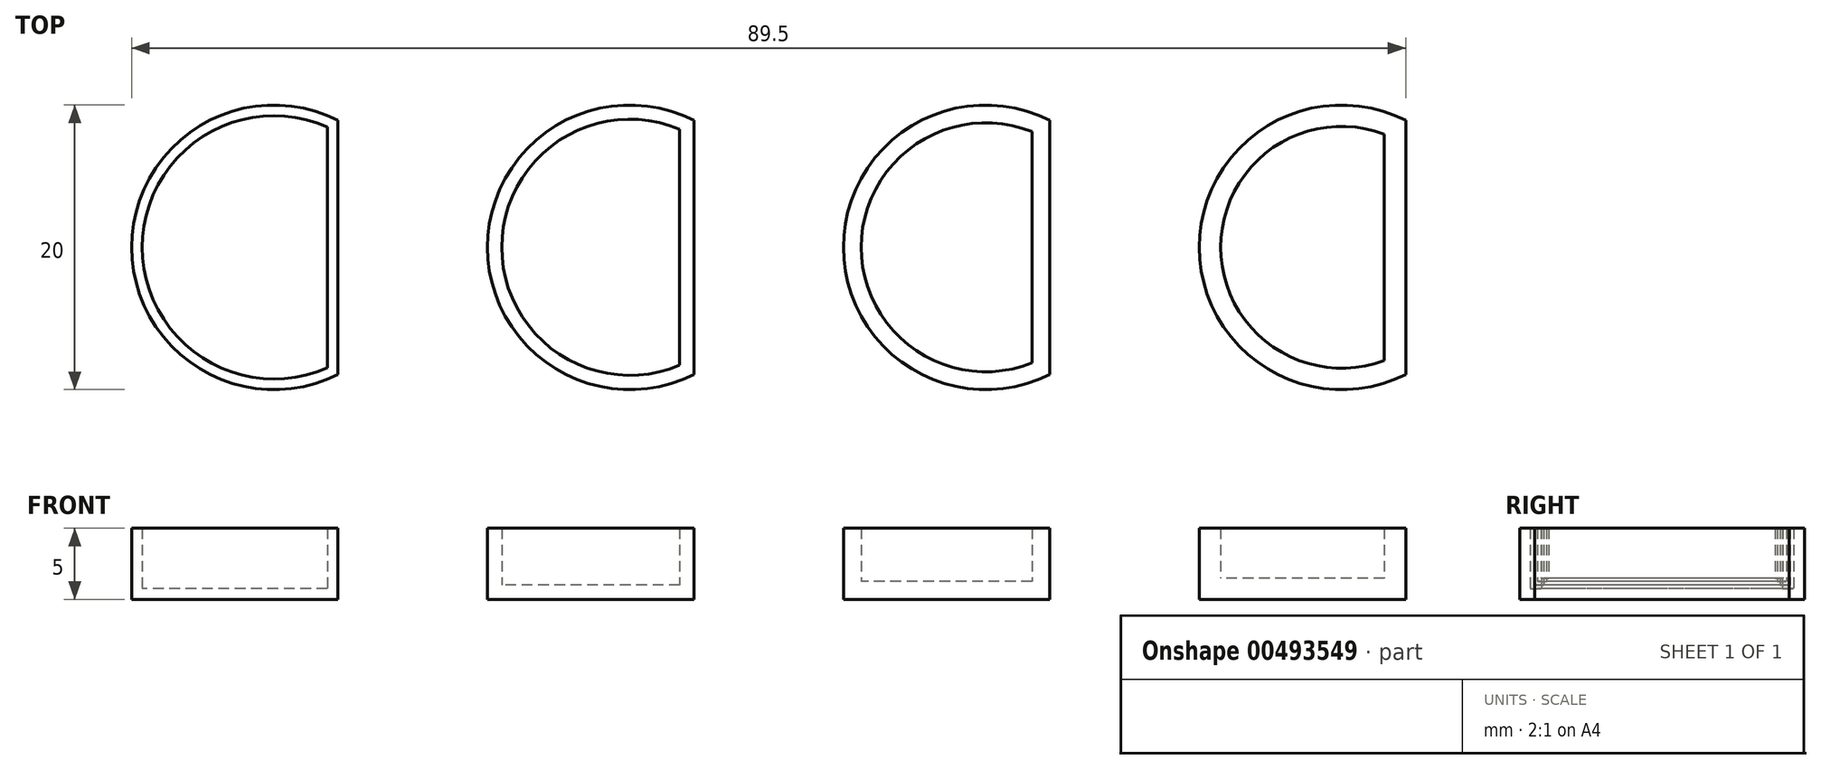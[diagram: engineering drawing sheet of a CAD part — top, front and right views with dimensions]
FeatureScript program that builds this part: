
annotation { "Feature Type Name" : "Feature", "Feature Type Description" : "" }
export const myFeature = defineFeature(function(context is Context, id is Id, definition is map)
    precondition{}
    {
        {
            var Q0;
            Q0=qCreatedBy(makeId("Top.planeOp"),FACE);
            var sketch = newSketch(context, id + "F0", { "sketchPlane" : qUnion([Q0])});
            skArc(sketch, "E0", {"start": v(-49.83, 50.8) * mm, "mid": v(-64.33, 41.87) * mm, "end": v(-49.83, 32.94) * mm});
            skLineSegment(sketch, "E1", {"start": v(-49.83, 50.8) * mm, "end": v(-49.83, 32.94) * mm});
            skArc(sketch, "E2.1.0.0", {"start": v(-24.83, 50.8) * mm, "mid": v(-39.33, 41.87) * mm, "end": v(-24.83, 32.94) * mm});
            skLineSegment(sketch, "E2.1.0.1", {"start": v(-24.83, 50.8) * mm, "end": v(-24.83, 32.94) * mm});
            skArc(sketch, "E2.2.0.0", {"start": v(0.17, 50.8) * mm, "mid": v(-14.33, 41.87) * mm, "end": v(0.17, 32.94) * mm});
            skLineSegment(sketch, "E2.2.0.1", {"start": v(0.17, 50.8) * mm, "end": v(0.17, 32.94) * mm});
            skArc(sketch, "E2.3.0.0", {"start": v(25.17, 50.8) * mm, "mid": v(10.67, 41.87) * mm, "end": v(25.17, 32.94) * mm});
            skLineSegment(sketch, "E2.3.0.1", {"start": v(25.17, 50.8) * mm, "end": v(25.17, 32.94) * mm});
            skLineSegment(sketch, "E2.direction1", {"start": v(-49.83, 32.94) * mm, "end": v(-24.83, 32.94) * mm, "construction": true});
            skSolve(sketch);
        }
        {
            var Q0;
            Q0=makeQuery(id+"F0.imprint","IMPRINT",FACE,{"disambiguationData":[TD([[makeQuery(id+"F0.imprint","IMPRINT",EDGE,{"derivedFrom":sQuery(id+"F0.wireOp",EDGE,"E0")}),1.0]])]});
            var Q1;
            Q1=makeQuery(id+"F0.imprint","IMPRINT",FACE,{"disambiguationData":[TD([[makeQuery(id+"F0.imprint","IMPRINT",EDGE,{"derivedFrom":sQuery(id+"F0.wireOp",EDGE,"E2.1.0.0")}),1.0]])]});
            var Q2;
            Q2=makeQuery(id+"F0.imprint","IMPRINT",FACE,{"disambiguationData":[TD([[makeQuery(id+"F0.imprint","IMPRINT",EDGE,{"derivedFrom":sQuery(id+"F0.wireOp",EDGE,"E2.2.0.0")}),1.0]])]});
            var Q3;
            Q3=makeQuery(id+"F0.imprint","IMPRINT",FACE,{"disambiguationData":[TD([[makeQuery(id+"F0.imprint","IMPRINT",EDGE,{"derivedFrom":sQuery(id+"F0.wireOp",EDGE,"E2.3.0.0")}),1.0]])]});
            extrude(context, id + "F1", {"entities" : qUnion([Q0, Q1, Q2, Q3]), "depth" : 5 * mm});
        }
        {
            var Q0;
            Q0=makeQuery(id+"F1.opExtrude","CAP_FACE",FACE,{"disambiguationData":[OSD([sQuery(id+"F0.wireOp",EDGE,"E0"),sQuery(id+"F0.wireOp",EDGE,"E1")])],"isStart":false});
            shell(context, id + "F2", {"entities" : qUnion([Q0]), "thickness" : .75 * mm});
        }
        {
            var Q0;
            Q0=makeQuery(id+"F1.opExtrude","CAP_FACE",FACE,{"disambiguationData":[OSD([sQuery(id+"F0.wireOp",EDGE,"E2.1.0.0"),sQuery(id+"F0.wireOp",EDGE,"E2.1.0.1")])],"isStart":false});
            shell(context, id + "F3", {"entities" : qUnion([Q0]), "thickness" : 1 * mm});
        }
        {
            var Q0;
            Q0=makeQuery(id+"F1.opExtrude","CAP_FACE",FACE,{"disambiguationData":[OSD([sQuery(id+"F0.wireOp",EDGE,"E2.2.0.0"),sQuery(id+"F0.wireOp",EDGE,"E2.2.0.1")])],"isStart":false});
            shell(context, id + "F4", {"entities" : qUnion([Q0]), "thickness" : 1.25 * mm});
        }
        {
            var Q0;
            Q0=makeQuery(id+"F1.opExtrude","CAP_FACE",FACE,{"disambiguationData":[OSD([sQuery(id+"F0.wireOp",EDGE,"E2.3.0.0"),sQuery(id+"F0.wireOp",EDGE,"E2.3.0.1")])],"isStart":false});
            shell(context, id + "F5", {"entities" : qUnion([Q0]), "thickness" : 1.5 * mm});
        }
    });
